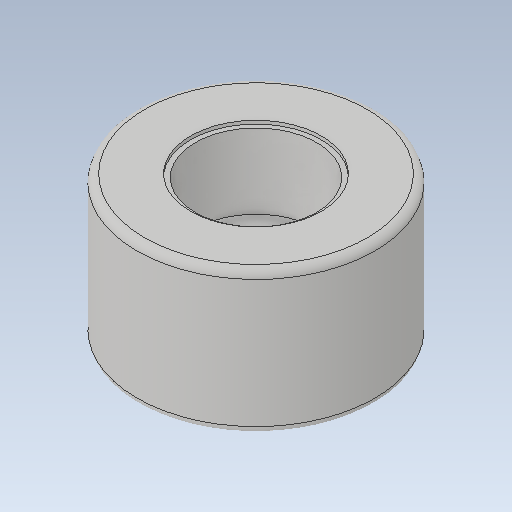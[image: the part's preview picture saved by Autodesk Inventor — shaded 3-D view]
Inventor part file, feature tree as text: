
AUTODESK INVENTOR PART (.ipt)
format: ipt  version: 2021 (Build 250183000, 183)  size: 181,248 bytes
history: native  units: in
note: dims shown in document units (in); Inventor stores cm internally (conversion verified against a paired STEP export)
features: fillet x1
ambient origin geometry x8: Origin, YZ Plane, XZ Plane, XY Plane, X Axis, Y Axis, Z Axis, Center Point
bodies: Solid1 (feature_tree)
feature tree (1):
  fillet  "Fillet1"  [1 undecoded]
note: 1 required parameter value undecoded (feature->parameter linkage not recoverable at this tier; creation-order binding heuristic only, values carry confidence <= 0.55)
